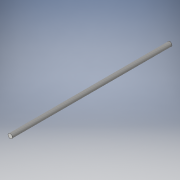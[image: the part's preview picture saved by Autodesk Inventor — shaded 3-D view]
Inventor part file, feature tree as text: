
AUTODESK INVENTOR PART (.ipt)
format: ipt  version: 2017.3 (Build 213256000, 256)  size: 92,672 bytes
history: native  units: in
note: dims shown in document units (in); Inventor stores cm internally (conversion verified against a paired STEP export)
features: extrude x1, thread x1, sketch x1
ambient origin geometry x8: Origin, YZ Plane, XZ Plane, XY Plane, X Axis, Y Axis, Z Axis, Center Point
bodies: Solid1 (feature_tree)
feature tree (3):
  extrude  "Extrusion1"  Depth=4.5in TaperAngle=0.0deg
  thread  "Thread1"  [1 undecoded]
  sketch  "Sketch1"  dims[d0=0.125in d1=4.5in d2=0.0in d3=1.0in d4=0.0in]
note: 1 required parameter value undecoded (feature->parameter linkage not recoverable at this tier; creation-order binding heuristic only, values carry confidence <= 0.55)
